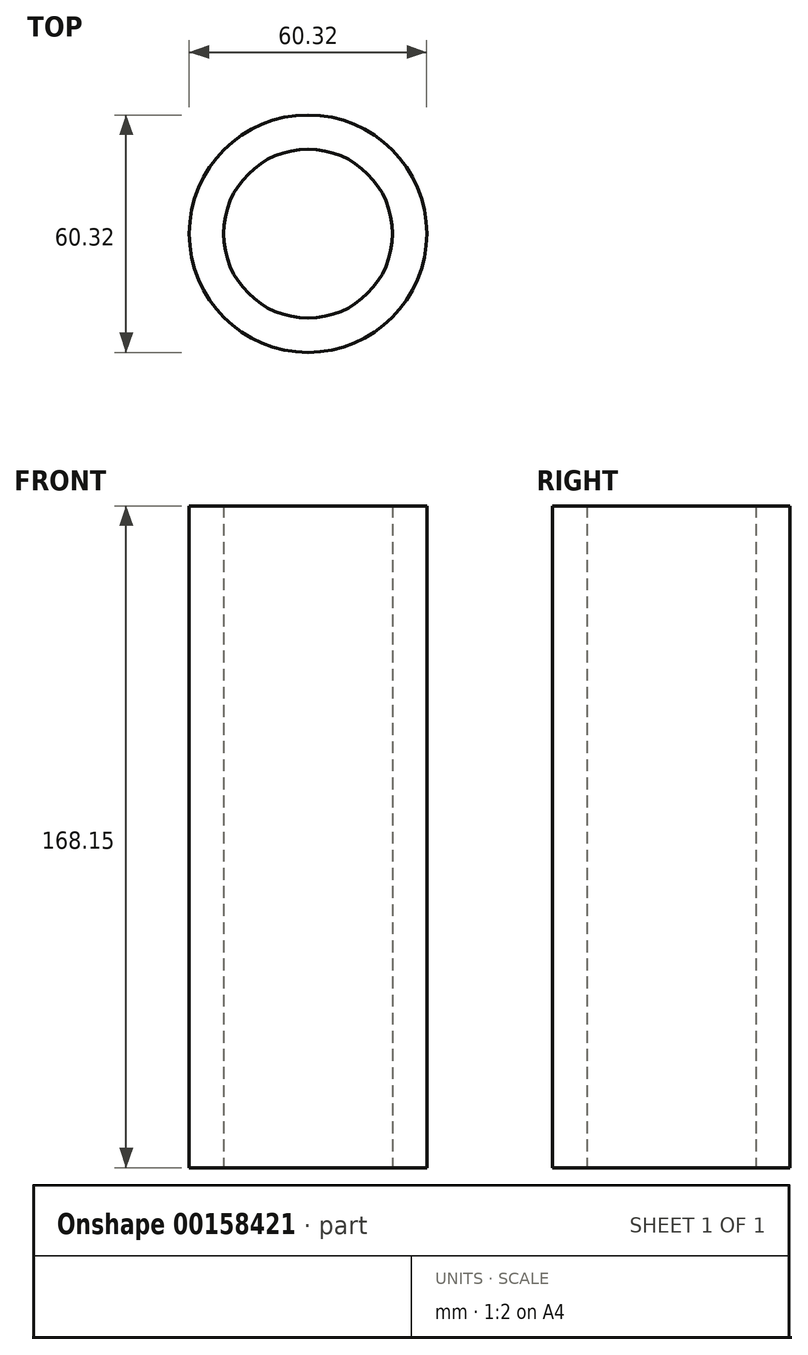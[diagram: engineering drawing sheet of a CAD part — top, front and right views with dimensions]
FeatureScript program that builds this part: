
annotation { "Feature Type Name" : "Feature", "Feature Type Description" : "" }
export const myFeature = defineFeature(function(context is Context, id is Id, definition is map)
    precondition{}
    {
        {
            var Q0;
            Q0=qCreatedBy(makeId("Top.planeOp"),FACE);
            var sketch = newSketch(context, id + "F0", { "sketchPlane" : qUnion([Q0])});
            skCircle(sketch, "E0", {"center": v(0, 0) * mm, "radius": 30.16 * mm});
            skCircle(sketch, "E1.0", {"center": v(0, 0) * mm, "radius": 21.45 * mm});
            skSolve(sketch);
        }
        {
            var Q0;
            Q0=makeQuery(id+"F0.imprint","IMPRINT",FACE,{"disambiguationData":[TD([[makeQuery(id+"F0.imprint","IMPRINT",EDGE,{"derivedFrom":sQuery(id+"F0.wireOp",EDGE,"E0")}),1.0]])]});
            extrude(context, id + "F1", {"entities" : qUnion([Q0]), "depth" : 168.15 * mm, "offsetDistance" : 25.4 * mm});
        }
    });
